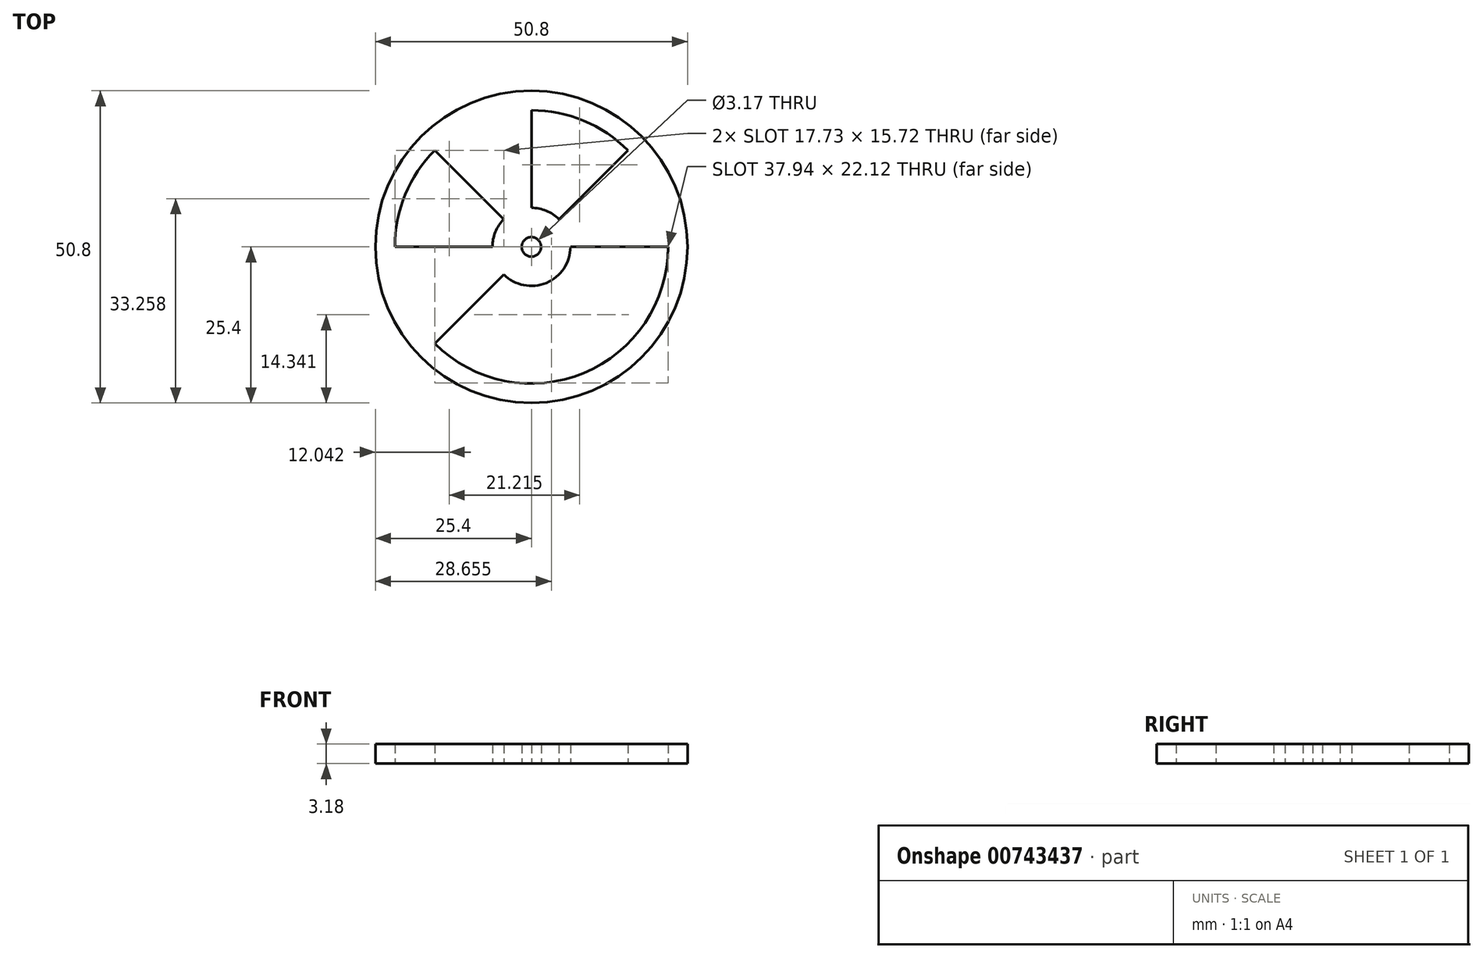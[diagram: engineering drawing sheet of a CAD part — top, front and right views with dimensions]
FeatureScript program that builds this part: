
annotation { "Feature Type Name" : "Feature", "Feature Type Description" : "" }
export const myFeature = defineFeature(function(context is Context, id is Id, definition is map)
    precondition{}
    {
        {
            var Q0;
            Q0=qCreatedBy(makeId("Top.planeOp"),FACE);
            var sketch = newSketch(context, id + "F0", { "sketchPlane" : qUnion([Q0])});
            skCircle(sketch, "E0", {"center": v(0, 0) * mm, "radius": 22.23 * mm});
            skCircle(sketch, "E1", {"center": v(0, 0) * mm, "radius": 6.35 * mm});
            skLineSegment(sketch, "E2", {"start": v(0, -6.35) * mm, "end": v(0, -22.23) * mm});
            skCircle(sketch, "E3", {"center": v(0, 0) * mm, "radius": 25.4 * mm});
            skLineSegment(sketch, "E4", {"start": v(-4.5, -4.5) * mm, "end": v(-15.72, -15.72) * mm});
            skLineSegment(sketch, "E5", {"start": v(-6.35, 0) * mm, "end": v(-22.23, 0) * mm});
            skLineSegment(sketch, "E6.MirrorCS", {"start": v(4.5, -4.5) * mm, "end": v(15.72, -15.72) * mm});
            skLineSegment(sketch, "E7.MirrorCS", {"start": v(6.35, 0) * mm, "end": v(22.23, 0) * mm});
            skLineSegment(sketch, "E8.MirrorCS", {"start": v(0, 6.35) * mm, "end": v(0, 22.23) * mm});
            skLineSegment(sketch, "E9.MirrorCS", {"start": v(-4.5, 4.5) * mm, "end": v(-15.72, 15.72) * mm});
            skLineSegment(sketch, "E10.MirrorCS", {"start": v(4.5, 4.5) * mm, "end": v(15.72, 15.72) * mm});
            skCircle(sketch, "E11", {"center": v(0, 0) * mm, "radius": 1.59 * mm});
            skSolve(sketch);
        }
        {
            var Q0;
            {var subQ0=sQuery(id+"F0.wireOp",EDGE,"E9.MirrorCS");Q0=makeQuery(id+"F0.imprint","IMPRINT",FACE,{"disambiguationData":[TD([[makeQuery(id+"F0.imprint","IMPRINT",EDGE,{"derivedFrom":subQ0}),-1.0]])]});}
            var Q1;
            {var subQ0=sQuery(id+"F0.wireOp",EDGE,"E10.MirrorCS");Q1=makeQuery(id+"F0.imprint","IMPRINT",FACE,{"disambiguationData":[TD([[makeQuery(id+"F0.imprint","IMPRINT",EDGE,{"derivedFrom":subQ0}),-1.0]])]});}
            var Q2;
            Q2=makeQuery(id+"F0.imprint","IMPRINT",FACE,{"disambiguationData":[TD([[makeQuery(id+"F0.imprint","IMPRINT",EDGE,{"derivedFrom":sQuery(id+"F0.wireOp",EDGE,"E3")}),1.0]])]});
            var Q3;
            Q3=makeQuery(id+"F0.imprint","IMPRINT",FACE,{"disambiguationData":[TD([[makeQuery(id+"F0.imprint","IMPRINT",EDGE,{"derivedFrom":sQuery(id+"F0.wireOp",EDGE,"E11")}),-1.0]])]});
            var Q4;
            {var subQ0=sQuery(id+"F0.wireOp",EDGE,"E6.MirrorCS");Q4=makeQuery(id+"F0.imprint","IMPRINT",FACE,{"disambiguationData":[TD([[makeQuery(id+"F0.imprint","IMPRINT",EDGE,{"derivedFrom":subQ0}),-1.0]])]});}
            var Q5;
            {var subQ0=sQuery(id+"F0.wireOp",EDGE,"E4");Q5=makeQuery(id+"F0.imprint","IMPRINT",FACE,{"disambiguationData":[TD([[makeQuery(id+"F0.imprint","IMPRINT",EDGE,{"derivedFrom":subQ0}),-1.0]])]});}
            extrude(context, id + "F1", {"entities" : qUnion([Q0, Q1, Q2, Q3, Q4, Q5]), "depth" : 3.17 * mm, "offsetDistance" : 25.4 * mm});
        }
    });
